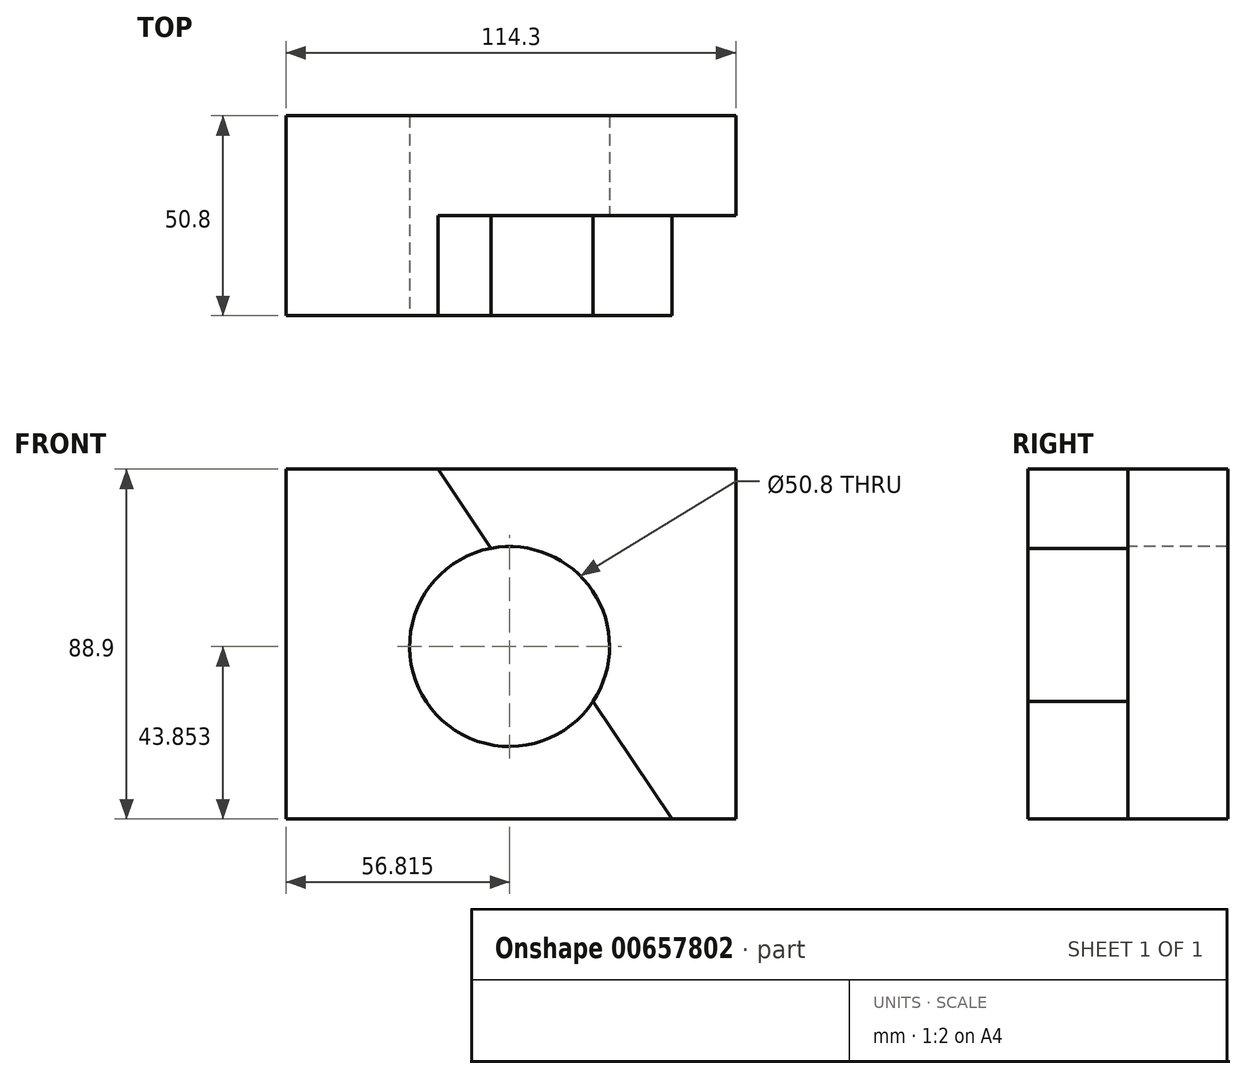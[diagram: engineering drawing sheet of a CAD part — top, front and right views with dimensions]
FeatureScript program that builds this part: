
annotation { "Feature Type Name" : "Feature", "Feature Type Description" : "" }
export const myFeature = defineFeature(function(context is Context, id is Id, definition is map)
    precondition{}
    {
        {
            var Q0;
            Q0=qCreatedBy(makeId("Top.planeOp"),FACE);
            var sketch = newSketch(context, id + "F0", { "sketchPlane" : qUnion([Q0])});
            skLineSegment(sketch, "E0.bottom", {"start": v(-20.04, -21.5) * mm, "end": v(94.26, -21.5) * mm});
            skLineSegment(sketch, "E0.top", {"start": v(-20.04, -72.3) * mm, "end": v(94.26, -72.3) * mm});
            skLineSegment(sketch, "E0.left", {"start": v(-20.04, -21.5) * mm, "end": v(-20.04, -72.3) * mm});
            skLineSegment(sketch, "E0.right", {"start": v(94.26, -21.5) * mm, "end": v(94.26, -72.3) * mm});
            skSolve(sketch);
        }
        {
            var Q0;
            Q0 = qSketchRegion(id + "F0", true);
            extrude(context, id + "F1", {"entities" : qUnion([Q0]), "depth" : 88.9 * mm, "offsetDistance" : 25.4 * mm});
        }
        {
            var Q0;
            Q0=makeQuery(id+"F1.opExtrude","SWEPT_FACE",FACE,{"disambiguationData":[OSD([sQuery(id+"F0.wireOp",EDGE,"E0.top")])]});
            var sketch = newSketch(context, id + "F2", { "sketchPlane" : qUnion([Q0])});
            skLineSegment(sketch, "E1.bottom", {"start": v(94.26, 0) * mm, "end": v(68.86, 0) * mm});
            skLineSegment(sketch, "E2", {"start": v(18.62, 88.9) * mm, "end": v(68.86, 0) * mm});
            skLineSegment(sketch, "E3", {"start": v(18.62, 88.9) * mm, "end": v(18.62, 0) * mm});
            skLineSegment(sketch, "E4", {"start": v(18.62, 0) * mm, "end": v(68.86, 0) * mm});
            skLineSegment(sketch, "E5", {"start": v(18.62, 88.9) * mm, "end": v(94.26, 88.9) * mm});
            skLineSegment(sketch, "E6", {"start": v(94.26, 88.9) * mm, "end": v(94.26, 0) * mm});
            skSolve(sketch);
        }
        {
            var Q0;
            Q0 = qSketchRegion(id + "F2", true);
            extrude(context, id + "F3", {"entities" : qUnion([Q0]), "operationType" : NewBodyOperationType.REMOVE, "oppositeDirection" : true, "depth" : 25.4 * mm, "offsetDistance" : 25.4 * mm});
        }
        {
            var Q0;
            Q0=makeQuery(id+"F3.boolean.opBoolean","COPY",FACE,{"derivedFrom":makeQuery(id+"F3.opExtrude","CAP_FACE",FACE,{"disambiguationData":[OSD([sQuery(id+"F2.wireOp",EDGE,"E3"),sQuery(id+"F2.wireOp",EDGE,"E4"),sQuery(id+"F2.wireOp",EDGE,"E5"),sQuery(id+"F2.wireOp",EDGE,"E6"),sQuery(id+"F2.wireOp",EDGE,"E1.bottom")])],"isStart":false})});
            var sketch = newSketch(context, id + "F4", { "sketchPlane" : qUnion([Q0])});
            skLineSegment(sketch, "E7", {"start": v(18.62, 88.9) * mm, "end": v(78, 0) * mm});
            skSolve(sketch);
        }
        {
            var Q0;
            Q0 = qSketchRegion(id + "F4", true);
            var Q1;
            {var subQ0=sQuery(id+"F4.wireOp",EDGE,"E7");Q1=makeQuery(id+"F4.imprint","IMPRINT",FACE,{"disambiguationData":[TD([[makeQuery(id+"F4.imprint","IMPRINT",EDGE,{"derivedFrom":subQ0}),-1.0]])]});}
            extrude(context, id + "F5", {"entities" : qUnion([Q0, Q1]), "operationType" : NewBodyOperationType.ADD, "depth" : 25.4 * mm, "offsetDistance" : 25.4 * mm});
        }
        {
            var Q0;
            Q0=makeQuery(id+"F5.boolean.opBoolean","MERGE",FACE,{"derivedFrom":[makeQuery(id+"F1.opExtrude","SWEPT_FACE",FACE,{"disambiguationData":[OSD([sQuery(id+"F0.wireOp",EDGE,"E0.top")])]}),makeQuery(id+"F5.opExtrude","CAP_FACE",FACE,{"disambiguationData":[OSD([sQuery(id+"F2.wireOp",EDGE,"E3"),sQuery(id+"F2.wireOp",EDGE,"E4"),sQuery(id+"F2.wireOp",EDGE,"E1.bottom"),sQuery(id+"F4.wireOp",EDGE,"E7")])],"isStart":false})]});
            var sketch = newSketch(context, id + "F6", { "sketchPlane" : qUnion([Q0])});
            skCircle(sketch, "E8", {"center": v(36.77, 43.85) * mm, "radius": 25.4 * mm});
            skSolve(sketch);
        }
        {
            var Q0;
            Q0 = qSketchRegion(id + "F6", true);
            extrude(context, id + "F7", {"entities" : qUnion([Q0]), "operationType" : NewBodyOperationType.REMOVE, "oppositeDirection" : true, "depth" : 92.2 * mm, "offsetDistance" : 25.4 * mm});
        }
    });
